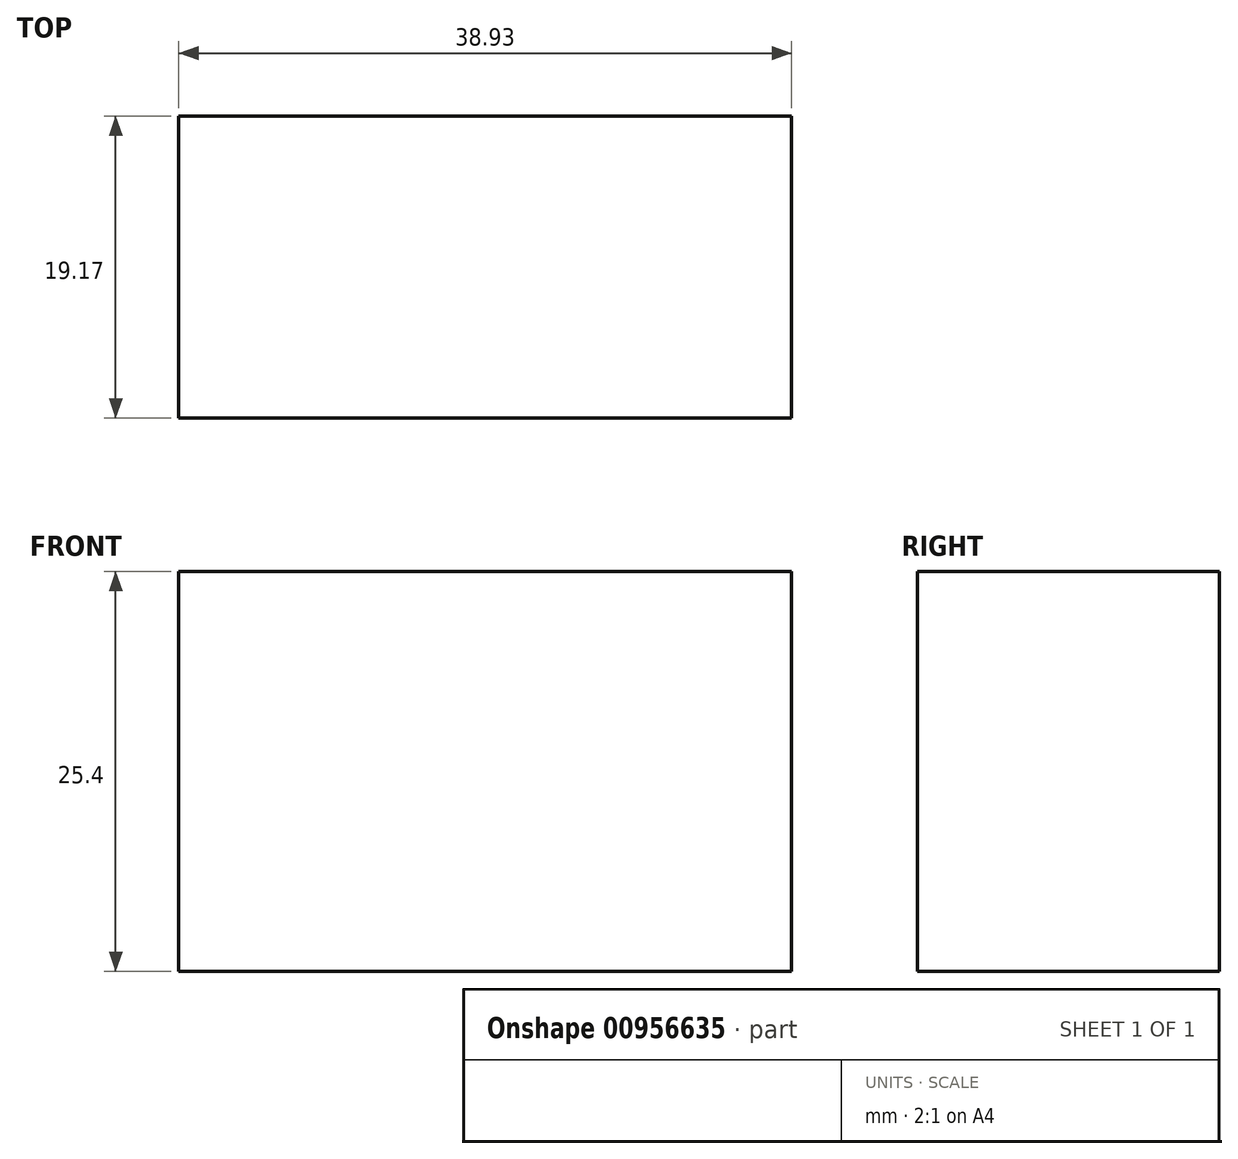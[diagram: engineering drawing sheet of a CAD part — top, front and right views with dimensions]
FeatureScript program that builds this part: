
annotation { "Feature Type Name" : "Feature", "Feature Type Description" : "" }
export const myFeature = defineFeature(function(context is Context, id is Id, definition is map)
    precondition{}
    {
        {
            var Q0;
            Q0=qCreatedBy(makeId("Top.planeOp"),FACE);
            var sketch = newSketch(context, id + "F0", { "sketchPlane" : qUnion([Q0])});
            skLineSegment(sketch, "E0.bottom", {"start": v(-68.8, 51.93) * mm, "end": v(-29.87, 51.93) * mm});
            skLineSegment(sketch, "E0.top", {"start": v(-68.8, 32.76) * mm, "end": v(-29.87, 32.76) * mm});
            skLineSegment(sketch, "E0.left", {"start": v(-68.8, 51.93) * mm, "end": v(-68.8, 32.76) * mm});
            skLineSegment(sketch, "E0.right", {"start": v(-29.87, 51.93) * mm, "end": v(-29.87, 32.76) * mm});
            skSolve(sketch);
        }
        {
            var Q0;
            Q0 = qSketchRegion(id + "F0", true);
            extrude(context, id + "F1", {"entities" : qUnion([Q0]), "depth" : 25.4 * mm, "offsetDistance" : 25.4 * mm});
        }
    });
